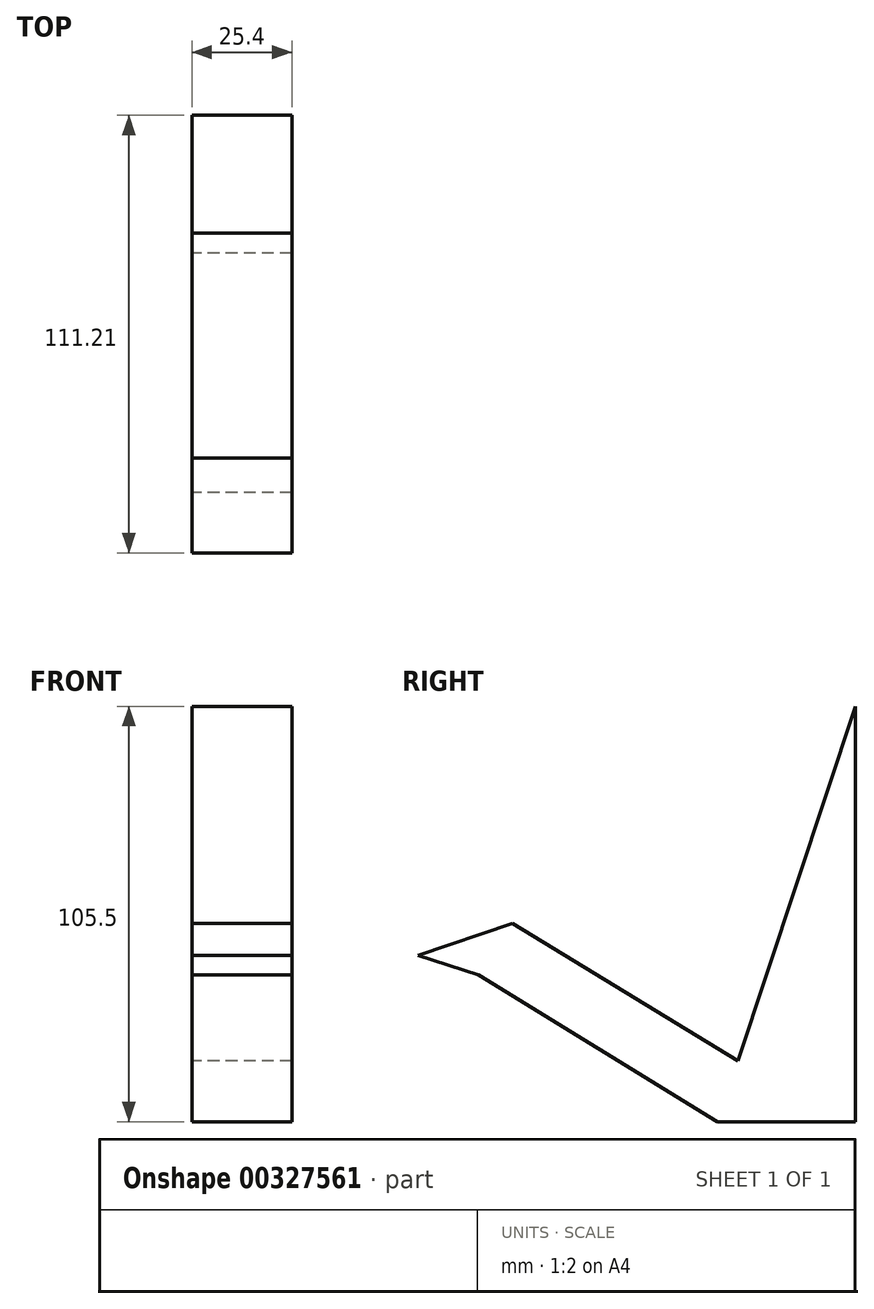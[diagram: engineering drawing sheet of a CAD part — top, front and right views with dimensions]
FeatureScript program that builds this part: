
annotation { "Feature Type Name" : "Feature", "Feature Type Description" : "" }
export const myFeature = defineFeature(function(context is Context, id is Id, definition is map)
    precondition{}
    {
        {
            var Q0;
            Q0=qCreatedBy(makeId("Right.planeOp"),FACE);
            var sketch = newSketch(context, id + "F0", { "sketchPlane" : qUnion([Q0])});
            skLineSegment(sketch, "E0", {"start": v(43.8, 54.7) * mm, "end": v(43.8, -50.79) * mm});
            skLineSegment(sketch, "E1", {"start": v(43.8, -50.79) * mm, "end": v(8.75, -50.79) * mm});
            skLineSegment(sketch, "E2", {"start": v(8.75, -50.79) * mm, "end": v(43.8, 54.7) * mm});
            skLineSegment(sketch, "E3", {"start": v(8.75, -50.79) * mm, "end": v(-52.03, -13.5) * mm});
            skLineSegment(sketch, "E4", {"start": v(-52.03, -13.5) * mm, "end": v(-43.75, 0) * mm});
            skLineSegment(sketch, "E5", {"start": v(-43.75, 0) * mm, "end": v(13.88, -35.36) * mm});
            skLineSegment(sketch, "E6", {"start": v(13.88, -35.36) * mm, "end": v(-43.35, -0.37) * mm});
            skLineSegment(sketch, "E7", {"start": v(-43.35, -0.37) * mm, "end": v(-67.41, -8.6) * mm});
            skLineSegment(sketch, "E8", {"start": v(-67.41, -8.6) * mm, "end": v(-52.03, -13.5) * mm});
            skLineSegment(sketch, "E9", {"start": v(-67.41, -8.6) * mm, "end": v(-67.41, -8.6) * mm});
            skSolve(sketch);
        }
        {
            var Q0;
            {var subQ2=sQuery(id+"F0.wireOp",EDGE,"E3");Q0=makeQuery(id+"F0.imprint","IMPRINT",FACE,{"disambiguationData":[TD([[makeQuery(id+"F0.imprint","IMPRINT",EDGE,{"derivedFrom":subQ2}),-1.0]])]});}
            var Q1;
            {var subQ0=sQuery(id+"F0.wireOp",EDGE,"E8");Q1=makeQuery(id+"F0.imprint","IMPRINT",FACE,{"disambiguationData":[TD([[makeQuery(id+"F0.imprint","IMPRINT",EDGE,{"derivedFrom":subQ0}),1.0]])]});}
            var Q2;
            {var subQ0=sQuery(id+"F0.wireOp",EDGE,"E0");Q2=makeQuery(id+"F0.imprint","IMPRINT",FACE,{"disambiguationData":[TD([[makeQuery(id+"F0.imprint","IMPRINT",EDGE,{"derivedFrom":subQ0}),-1.0]])]});}
            extrude(context, id + "F1", {"entities" : qUnion([Q0, Q1, Q2]), "depth" : 25.4 * mm});
        }
    });
